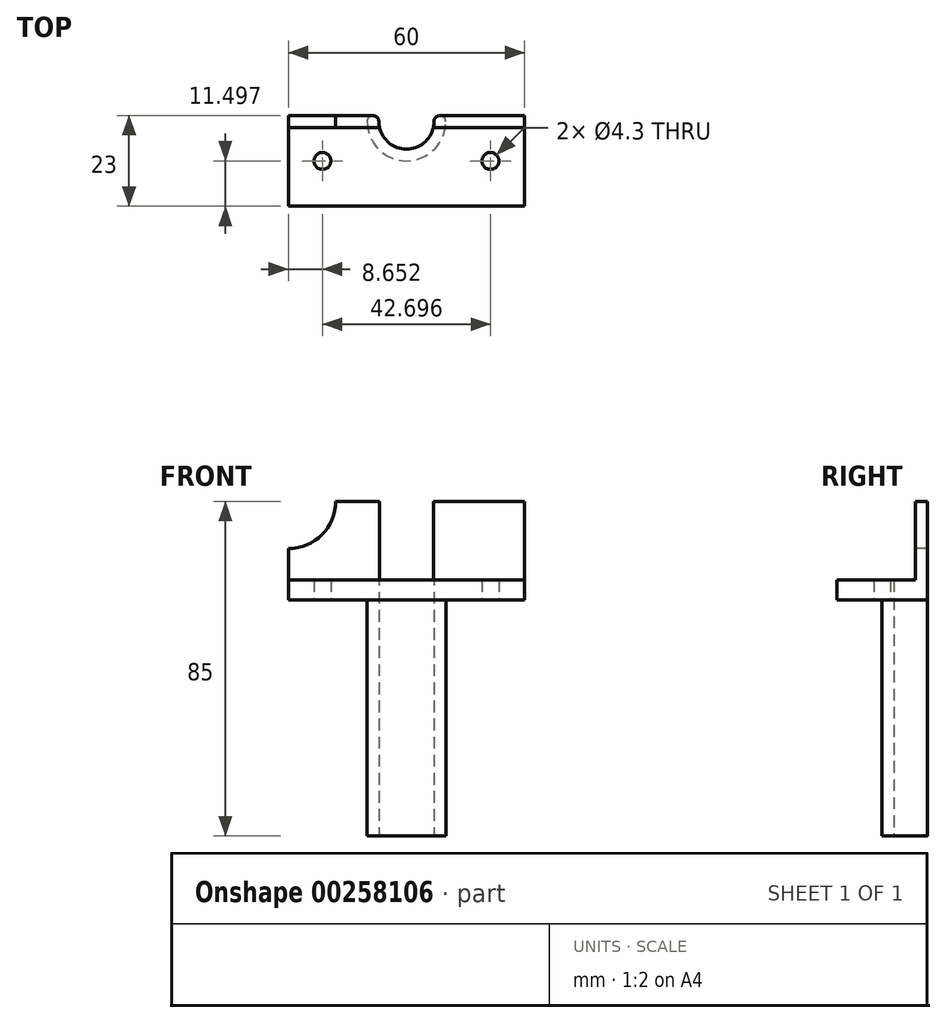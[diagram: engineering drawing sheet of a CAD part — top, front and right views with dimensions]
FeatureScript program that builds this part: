
annotation { "Feature Type Name" : "Feature", "Feature Type Description" : "" }
export const myFeature = defineFeature(function(context is Context, id is Id, definition is map)
    precondition{}
    {
        {
            var Q0;
            Q0=qCreatedBy(makeId("Top.planeOp"),FACE);
            var sketch = newSketch(context, id + "F0", { "sketchPlane" : qUnion([Q0])});
            skLineSegment(sketch, "E0.bottom", {"start": v(-30, 6.13) * mm, "end": v(30, 6.13) * mm});
            skLineSegment(sketch, "E0.top", {"start": v(-30, -16.87) * mm, "end": v(30, -16.87) * mm});
            skLineSegment(sketch, "E0.left", {"start": v(-30, 6.13) * mm, "end": v(-30, -16.87) * mm});
            skLineSegment(sketch, "E0.right", {"start": v(30, 6.13) * mm, "end": v(30, -16.87) * mm});
            skPoint(sketch, "E0.middle", {"position": v(0, 4.63) * mm});
            skLineSegment(sketch, "E1.top", {"start": v(-8, 6.13) * mm, "end": v(8, 6.13) * mm});
            skCircle(sketch, "E2", {"center": v(-21.35, -5.37) * mm, "radius": 2.15 * mm});
            skCircle(sketch, "E3", {"center": v(21.35, -5.37) * mm, "radius": 2.15 * mm});
            skArc(sketch, "E4", {"start": v(-10, 4.63) * mm, "mid": v(0, -5.37) * mm, "end": v(10, 4.63) * mm});
            skArc(sketch, "E5.0", {"start": v(-7, 4.63) * mm, "mid": v(0, -2.37) * mm, "end": v(7, 4.63) * mm});
            skArc(sketch, "E6", {"start": v(-10, 4.63) * mm, "mid": v(-8.5, 6.13) * mm, "end": v(-7, 4.63) * mm});
            skArc(sketch, "E7", {"start": v(7, 4.63) * mm, "mid": v(8.5, 6.13) * mm, "end": v(10, 4.63) * mm});
            skSolve(sketch);
        }
        {
            var Q0;
            {var subQ4=sQuery(id+"F0.wireOp",EDGE,"E1.bottom");Q0=makeQuery(id+"F0.imprint","IMPRINT",FACE,{"disambiguationData":[TD([[makeQuery(id+"F0.imprint","IMPRINT",EDGE,{"derivedFrom":subQ4}),-1.0]])]});}
            var Q1;
            {var subQ0=sQuery(id+"F0.wireOp",EDGE,"7Dd0WmuN-LdLT-SVaT-xg1O-Vh4xgTE7dWRA");Q1=makeQuery(id+"F0.imprint","IMPRINT",FACE,{"disambiguationData":[TD([[makeQuery(id+"F0.imprint","IMPRINT",EDGE,{"derivedFrom":subQ0}),-1.0]])]});}
            var Q2;
            {var subQ0=sQuery(id+"F0.wireOp",EDGE,"mgxlfd0t-O7RN-lP6g-sUdB-ZEcnTz3PzKJt");Q2=makeQuery(id+"F0.imprint","IMPRINT",FACE,{"disambiguationData":[TD([[makeQuery(id+"F0.imprint","IMPRINT",EDGE,{"derivedFrom":subQ0}),-1.0]])]});}
            var Q3;
            Q3=makeQuery(id+"F0.imprint","IMPRINT",FACE,{"disambiguationData":[TD([[makeQuery(id+"F0.imprint","IMPRINT",EDGE,{"derivedFrom":sQuery(id+"F0.wireOp",EDGE,"E0.top")}),1.0]])]});
            var Q4;
            Q4=makeQuery(id+"F0.imprint","IMPRINT",FACE,{"disambiguationData":[TD([[makeQuery(id+"F0.imprint","IMPRINT",EDGE,{"derivedFrom":sQuery(id+"F0.wireOp",EDGE,"E4")}),1.0]])]});
            var Q5;
            {var subQ0=sQuery(id+"F0.wireOp",EDGE,"E1.top");Q5=makeQuery(id+"F0.imprint","IMPRINT",FACE,{"disambiguationData":[TD([[makeQuery(id+"F0.imprint","IMPRINT",EDGE,{"derivedFrom":subQ0}),-1.0]])]});}
            extrude(context, id + "F1", {"entities" : qUnion([Q0, Q1, Q2, Q3, Q4, Q5]), "depth" : 5 * mm, "offsetDistance" : 25 * mm});
        }
        {
            var Q0;
            Q0=makeQuery(id+"F1.opExtrude","CAP_FACE",FACE,{"disambiguationData":[OSD([sQuery(id+"F0.wireOp",EDGE,"E0.top"),sQuery(id+"F0.wireOp",EDGE,"E0.left"),sQuery(id+"F0.wireOp",EDGE,"E0.right"),sQuery(id+"F0.wireOp",EDGE,"E1.bottom"),sQuery(id+"F0.wireOp",EDGE,"E1.left"),sQuery(id+"F0.wireOp",EDGE,"E1.right"),sQuery(id+"F0.wireOp",EDGE,"7Dd0WmuN-LdLT-SVaT-xg1O-Vh4xgTE7dWRA"),sQuery(id+"F0.wireOp",EDGE,"mgxlfd0t-O7RN-lP6g-sUdB-ZEcnTz3PzKJt")])],"isStart":false});
            var sketch = newSketch(context, id + "F2", { "sketchPlane" : qUnion([Q0])});
            skLineSegment(sketch, "E8.bottom", {"start": v(-30, 6.13) * mm, "end": v(30, 6.13) * mm});
            skLineSegment(sketch, "E8.top", {"start": v(-30, 3.13) * mm, "end": v(30, 3.13) * mm});
            skLineSegment(sketch, "E8.left", {"start": v(-30, 6.13) * mm, "end": v(-30, 3.13) * mm});
            skLineSegment(sketch, "E8.right", {"start": v(30, 6.13) * mm, "end": v(30, 3.13) * mm});
            skSolve(sketch);
        }
        {
            var Q0;
            Q0=makeQuery(id+"F2.imprint","IMPRINT",FACE,{"disambiguationData":[TD([[makeQuery(id+"F2.imprint","IMPRINT",EDGE,{"derivedFrom":sQuery(id+"F2.wireOp",EDGE,"E8.bottom")}),-1.0]])]});
            extrude(context, id + "F3", {"entities" : qUnion([Q0]), "operationType" : NewBodyOperationType.ADD, "depth" : 20 * mm});
        }
        {
            var Q0;
            Q0=makeQuery(id+"F3.opExtrude","SWEPT_FACE",FACE,{"disambiguationData":[OSD([sQuery(id+"F2.wireOp",EDGE,"E8.top")])]});
            var sketch = newSketch(context, id + "F4", { "sketchPlane" : qUnion([Q0])});
            skArc(sketch, "E9", {"start": v(-30, 13) * mm, "mid": v(-21.51, 16.51) * mm, "end": v(-18, 25) * mm});
            skArc(sketch, "E10", {"start": v(18, 25) * mm, "mid": v(21.51, 16.51) * mm, "end": v(30, 13) * mm});
            skSolve(sketch);
        }
        {
            var Q0;
            {var subQ0=sQuery(id+"F4.wireOp",EDGE,"E9");Q0=makeQuery(id+"F4.imprint","IMPRINT",FACE,{"disambiguationData":[TD([[makeQuery(id+"F4.imprint","IMPRINT",EDGE,{"derivedFrom":subQ0}),1.0]])]});}
            var Q1;
            {var subQ0=sQuery(id+"F4.wireOp",EDGE,"E10");Q1=makeQuery(id+"F4.imprint","IMPRINT",FACE,{"disambiguationData":[TD([[makeQuery(id+"F4.imprint","IMPRINT",EDGE,{"derivedFrom":subQ0}),1.0]])]});}
            extrude(context, id + "F5", {"entities" : qUnion([Q0, Q1]), "operationType" : NewBodyOperationType.REMOVE, "oppositeDirection" : true, "depth" : 4 * mm});
        }
        {
            var Q0;
            Q0=makeQuery(id+"F0.imprint","IMPRINT",FACE,{"disambiguationData":[TD([[makeQuery(id+"F0.imprint","IMPRINT",EDGE,{"derivedFrom":sQuery(id+"F0.wireOp",EDGE,"E4")}),1.0]])]});
            extrude(context, id + "F6", {"entities" : qUnion([Q0]), "operationType" : NewBodyOperationType.ADD, "oppositeDirection" : true, "depth" : 60 * mm, "offsetDistance" : 25 * mm});
        }
        {
            var Q0;
            Q0=makeQuery(id+"F6.opExtrude","CAP_FACE",FACE,{"disambiguationData":[OSD([sQuery(id+"F0.wireOp",EDGE,"E4"),sQuery(id+"F0.wireOp",EDGE,"E5.0"),sQuery(id+"F0.wireOp",EDGE,"E6"),sQuery(id+"F0.wireOp",EDGE,"E7")])],"isStart":false});
            var sketch = newSketch(context, id + "F7", { "sketchPlane" : qUnion([Q0])});
            skArc(sketch, "E11.0", {"start": v(-20, -4.63) * mm, "mid": v(0, 15.37) * mm, "end": v(20, -4.63) * mm});
            skLineSegment(sketch, "E12", {"start": v(-20, -4.63) * mm, "end": v(-7, -4.63) * mm});
            skLineSegment(sketch, "E13", {"start": v(7, -4.63) * mm, "end": v(20, -4.63) * mm});
            skSolve(sketch);
        }
        {
            var Q0;
            Q0 = qSketchRegion(id + "F7", true);
            var Q1;
            {var subQ0=sQuery(id+"F7.wireOp",EDGE,"E11.0");Q1=makeQuery(id+"F7.imprint","IMPRINT",FACE,{"disambiguationData":[TD([[makeQuery(id+"F7.imprint","IMPRINT",EDGE,{"derivedFrom":subQ0}),-1.0]])]});}
            var Q2;
            {var subQ2=makeQuery(id+"F6.opExtrude","CAP_EDGE",EDGE,{"disambiguationData":[OSD([sQuery(id+"F0.wireOp",EDGE,"E4")])],"isStart":false});Q2=makeQuery(id+"F7.imprint","IMPRINT",FACE,{"disambiguationData":[TD([[makeQuery(id+"F7.imprint","IMPRINT",EDGE,{"derivedFrom":subQ2}),-1.0]])]});}
            extrude(context, id + "F8", {"entities" : qUnion([Q0, Q1, Q2]), "operationType" : NewBodyOperationType.ADD, "oppositeDirection" : true, "depth" : 3 * mm, "offsetDistance" : 25 * mm});
        }
    });
